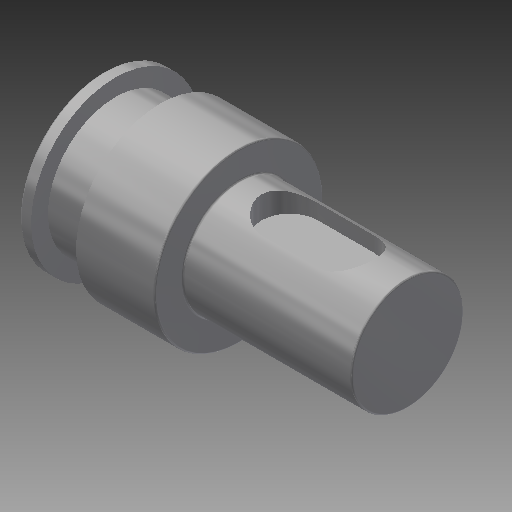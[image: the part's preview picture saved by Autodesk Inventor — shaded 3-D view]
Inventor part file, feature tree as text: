
AUTODESK INVENTOR PART (.ipt)
format: ipt  version: 2019.4 (Build 234330000, 330)  size: 209,920 bytes
history: native  units: mm
features: other x8, fillet x4
ambient origin geometry x6: Origin, XZ Plane, XY Plane, X Axis, Y Axis, Z Axis
bodies: Body1 (feature_tree)
feature tree (12):
  other  "實體1"
  other  "迴轉1"
  other  "鍵槽1"
  other  "扣環槽2"
  fillet  "圓角1"  [1 undecoded]
  fillet  "圓角2"  Radius=15.0mm
  fillet  "圓角3"  Radius=10.0mm
  fillet  "圓角4"  [1 undecoded]
  other  "起始平面"
  other  "主要草圖"
  other  "iFeature27:2"
  other  "iFeature3:1"
note: 2 required parameter values undecoded (feature->parameter linkage not recoverable at this tier; creation-order binding heuristic only, values carry confidence <= 0.55)
